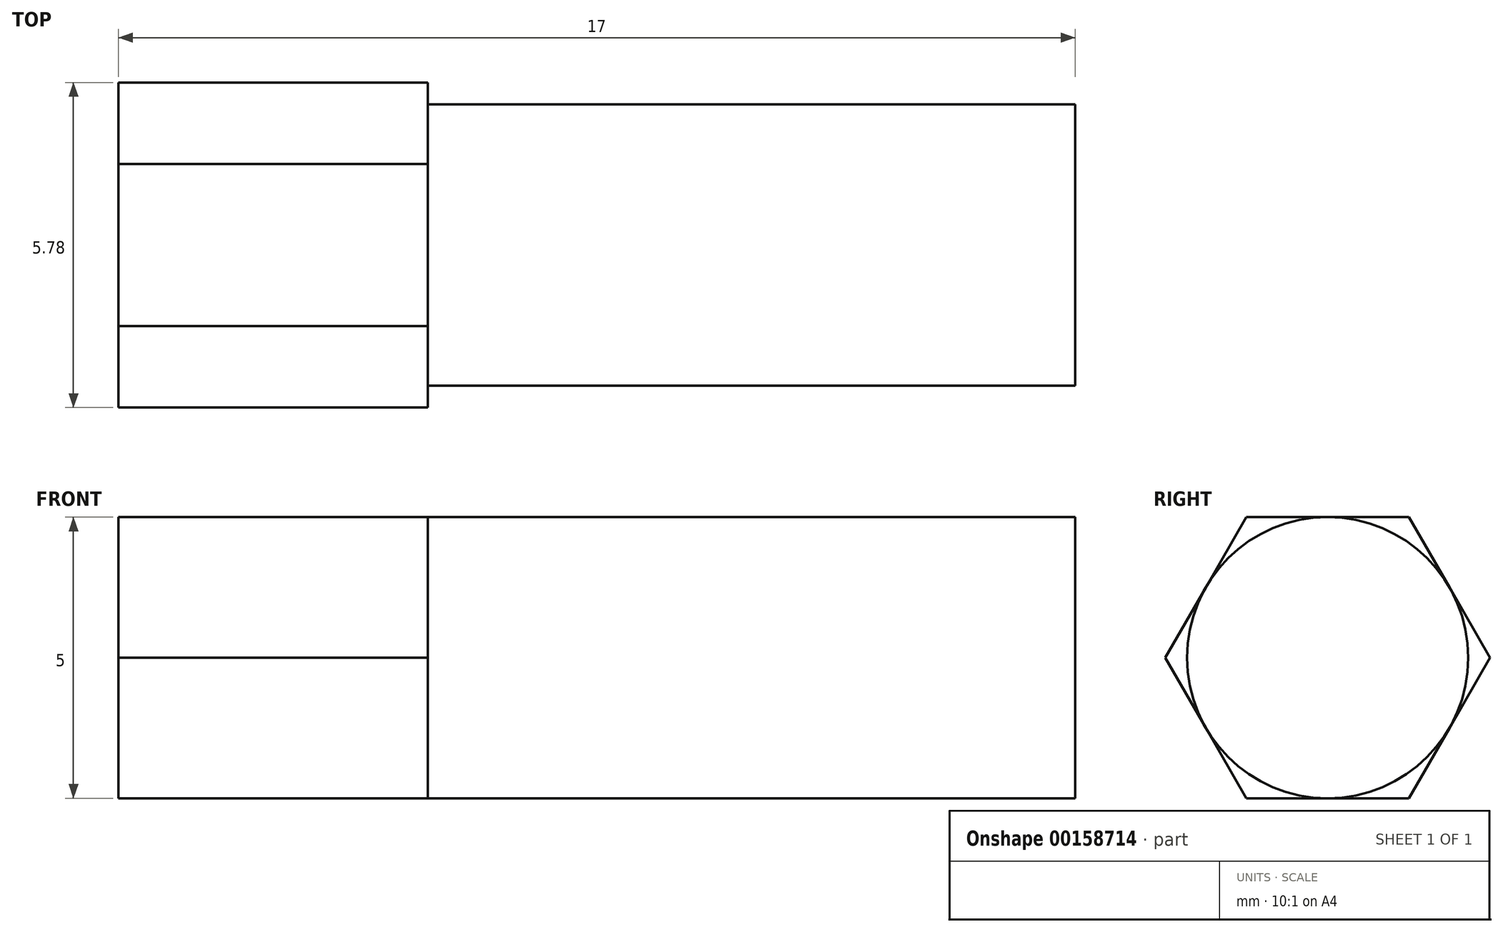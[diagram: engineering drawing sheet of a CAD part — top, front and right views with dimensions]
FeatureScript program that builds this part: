
annotation { "Feature Type Name" : "Feature", "Feature Type Description" : "" }
export const myFeature = defineFeature(function(context is Context, id is Id, definition is map)
    precondition{}
    {
        {
            var Q0;
            Q0=qCreatedBy(makeId("Right.planeOp"),FACE);
            var sketch = newSketch(context, id + "F0", { "sketchPlane" : qUnion([Q0])});
            skCircle(sketch, "E0.cCircle", {"center": v(0, 0) * mm, "radius": 2.5 * mm, "construction": true});
            skLineSegment(sketch, "E0.0", {"start": v(-1.44, 2.5) * mm, "end": v(1.44, 2.5) * mm});
            skLineSegment(sketch, "E0.1", {"start": v(1.44, 2.5) * mm, "end": v(2.89, 0) * mm});
            skLineSegment(sketch, "E0.2", {"start": v(2.89, 0) * mm, "end": v(1.44, -2.5) * mm});
            skLineSegment(sketch, "E0.3", {"start": v(1.44, -2.5) * mm, "end": v(-1.44, -2.5) * mm});
            skLineSegment(sketch, "E0.4", {"start": v(-1.44, -2.5) * mm, "end": v(-2.89, 0) * mm});
            skLineSegment(sketch, "E0.5", {"start": v(-2.89, 0) * mm, "end": v(-1.44, 2.5) * mm});
            skPoint(sketch, "E0.0.midPoint", {"position": v(0, 2.5) * mm});
            skSolve(sketch);
        }
        {
            var Q0;
            Q0 = qSketchRegion(id + "F0", true);
            extrude(context, id + "F1", {"entities" : qUnion([Q0]), "depth" : 5.5 * mm});
        }
        {
            var Q0;
            Q0=makeQuery(id+"F1.opExtrude","CAP_FACE",FACE,{"disambiguationData":[OSD([sQuery(id+"F0.wireOp",EDGE,"E0.0"),sQuery(id+"F0.wireOp",EDGE,"E0.1"),sQuery(id+"F0.wireOp",EDGE,"E0.2"),sQuery(id+"F0.wireOp",EDGE,"E0.3"),sQuery(id+"F0.wireOp",EDGE,"E0.4"),sQuery(id+"F0.wireOp",EDGE,"E0.5")])],"isStart":false});
            var sketch = newSketch(context, id + "F2", { "sketchPlane" : qUnion([Q0])});
            skCircle(sketch, "E1", {"center": v(0, 0) * mm, "radius": 2.5 * mm});
            skSolve(sketch);
        }
        {
            var Q0;
            {var subQ0=sQuery(id+"F2.wireOp",EDGE,"E1");var subQ4=makeQuery(id+"F2.imprint","INTERSECT",VERTEX,{"derivedFrom":[makeQuery(id+"F1.opExtrude","CAP_EDGE",EDGE,{"disambiguationData":[OSD([sQuery(id+"F0.wireOp",EDGE,"E0.0")])],"isStart":false}),subQ0]});Q0=makeQuery(id+"F2.imprint","IMPRINT",FACE,{"disambiguationData":[TD([[makeQuery(id+"F2.imprint","IMPRINT",EDGE,{"disambiguationData":[TD([[subQ4,1.0]])],"derivedFrom":subQ0}),1.0]])]});}
            extrude(context, id + "F3", {"entities" : qUnion([Q0]), "operationType" : NewBodyOperationType.ADD, "depth" : 11.5 * mm});
        }
    });
